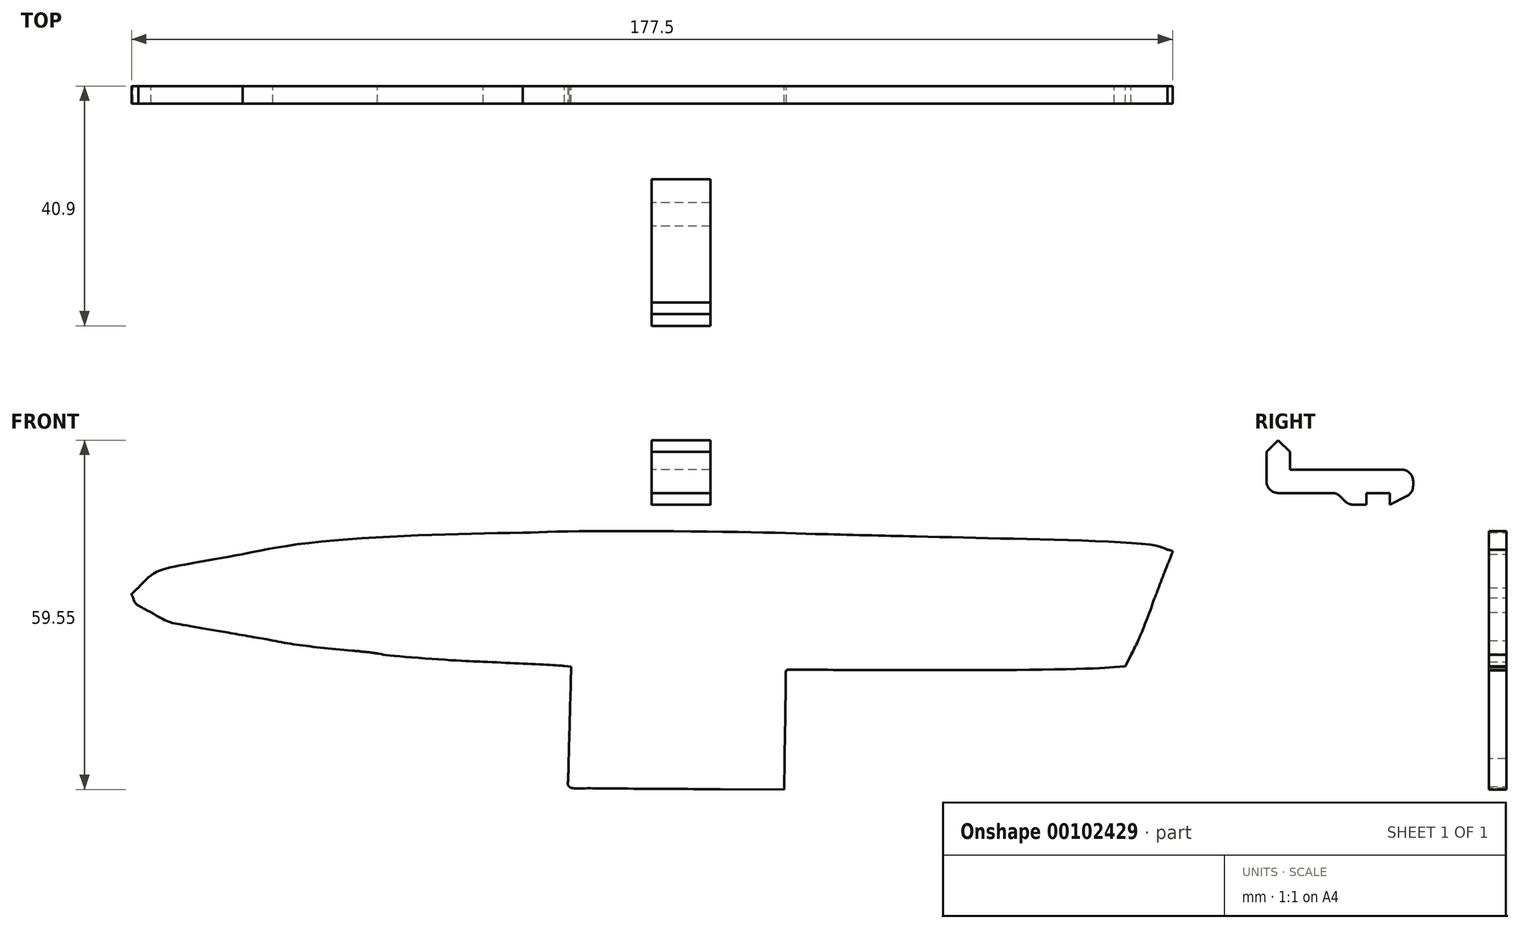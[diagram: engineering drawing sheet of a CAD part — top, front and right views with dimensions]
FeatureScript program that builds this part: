
annotation { "Feature Type Name" : "Feature", "Feature Type Description" : "" }
export const myFeature = defineFeature(function(context is Context, id is Id, definition is map)
    precondition{}
    {
        {
            var Q0;
            Q0=qCreatedBy(makeId("Right.planeOp"),FACE);
            var sketch = newSketch(context, id + "F0", { "sketchPlane" : qUnion([Q0])});
            skLineSegment(sketch, "E0.bottom", {"start": v(-15.9, 32.6) * mm, "end": v(-40.9, 32.6) * mm});
            skLineSegment(sketch, "E0.top", {"start": v(-15.9, 28.6) * mm, "end": v(-40.9, 28.6) * mm});
            skLineSegment(sketch, "E0.left", {"start": v(-15.9, 32.6) * mm, "end": v(-15.9, 28.6) * mm});
            skLineSegment(sketch, "E0.right", {"start": v(-40.9, 32.6) * mm, "end": v(-40.9, 28.6) * mm});
            skLineSegment(sketch, "E1", {"start": v(-15.9, 28.6) * mm, "end": v(-19.9, 26.6) * mm});
            skLineSegment(sketch, "E2", {"start": v(-19.9, 26.6) * mm, "end": v(-19.9, 28.6) * mm});
            skLineSegment(sketch, "E3", {"start": v(-23.9, 28.6) * mm, "end": v(-23.9, 26.6) * mm});
            skLineSegment(sketch, "E4", {"start": v(-23.9, 26.6) * mm, "end": v(-26.9, 26.6) * mm});
            skLineSegment(sketch, "E5", {"start": v(-26.9, 26.6) * mm, "end": v(-28.9, 28.6) * mm});
            skLineSegment(sketch, "E6", {"start": v(-40.9, 32.6) * mm, "end": v(-40.9, 37.6) * mm});
            skLineSegment(sketch, "E7", {"start": v(-40.9, 37.6) * mm, "end": v(-36.9, 37.6) * mm});
            skLineSegment(sketch, "E8", {"start": v(-36.9, 37.6) * mm, "end": v(-36.9, 32.6) * mm});
            skSolve(sketch);
        }
        {
            var Q0;
            Q0=makeQuery(id+"F0.imprint","IMPRINT",FACE,{"disambiguationData":[TD([[makeQuery(id+"F0.imprint","IMPRINT",EDGE,{"derivedFrom":sQuery(id+"F0.wireOp",EDGE,"E0.bottom")}),1.0]])]});
            var Q1;
            {var subQ2=sQuery(id+"F0.wireOp",EDGE,"E3");Q1=makeQuery(id+"F0.imprint","IMPRINT",FACE,{"disambiguationData":[TD([[makeQuery(id+"F0.imprint","IMPRINT",EDGE,{"derivedFrom":subQ2}),-1.0]])]});}
            var Q2;
            {var subQ0=sQuery(id+"F0.wireOp",EDGE,"E1");Q2=makeQuery(id+"F0.imprint","IMPRINT",FACE,{"disambiguationData":[TD([[makeQuery(id+"F0.imprint","IMPRINT",EDGE,{"derivedFrom":subQ0}),-1.0]])]});}
            var Q3;
            {var subQ0=sQuery(id+"F0.wireOp",EDGE,"E6");Q3=makeQuery(id+"F0.imprint","IMPRINT",FACE,{"disambiguationData":[TD([[makeQuery(id+"F0.imprint","IMPRINT",EDGE,{"derivedFrom":subQ0}),-1.0]])]});}
            extrude(context, id + "F1", {"entities" : qUnion([Q0, Q1, Q2, Q3]), "depth" : 10 * mm, "offsetDistance" : 25 * mm});
        }
        {
            var Q0;
            Q0=makeQuery(id+"F1.opExtrude","SWEPT_EDGE",EDGE,{"disambiguationData":[OSD([sQuery(id+"F0.wireOp",EDGE,"E0.top"),sQuery(id+"F0.wireOp",EDGE,"E0.left"),sQuery(id+"F0.wireOp",EDGE,"E1")])]});
            var Q1;
            Q1=makeQuery(id+"F1.opExtrude","SWEPT_EDGE",EDGE,{"disambiguationData":[OSD([sQuery(id+"F0.wireOp",EDGE,"E4"),sQuery(id+"F0.wireOp",EDGE,"E5")])]});
            var Q2;
            Q2=makeQuery(id+"F1.opExtrude","SWEPT_EDGE",EDGE,{"disambiguationData":[OSD([sQuery(id+"F0.wireOp",EDGE,"E0.top"),sQuery(id+"F0.wireOp",EDGE,"E5")])]});
            var Q3;
            Q3=makeQuery(id+"F1.opExtrude","SWEPT_EDGE",EDGE,{"disambiguationData":[OSD([sQuery(id+"F0.wireOp",EDGE,"E0.top"),sQuery(id+"F0.wireOp",EDGE,"E0.right")])]});
            var Q4;
            Q4=makeQuery(id+"F1.opExtrude","SWEPT_EDGE",EDGE,{"disambiguationData":[OSD([sQuery(id+"F0.wireOp",EDGE,"E0.bottom"),sQuery(id+"F0.wireOp",EDGE,"E0.left")])]});
            fillet(context, id + "F2", {"entities" : qUnion([Q0, Q1, Q2, Q3, Q4]), "tangentPropagation" : true, "radius" : 2 * mm, "defaultsChanged" : false, "vertexSettings" : [], "allowEdgeOverflow" : false});
        }
        {
            var Q0;
            Q0=makeQuery(id+"F1.opExtrude","SWEPT_EDGE",EDGE,{"disambiguationData":[OSD([sQuery(id+"F0.wireOp",EDGE,"E7"),sQuery(id+"F0.wireOp",EDGE,"E8")])]});
            var Q1;
            Q1=makeQuery(id+"F1.opExtrude","SWEPT_EDGE",EDGE,{"disambiguationData":[OSD([sQuery(id+"F0.wireOp",EDGE,"E6"),sQuery(id+"F0.wireOp",EDGE,"E7")])]});
            chamfer(context, id + "F3", {"entities" : qUnion([Q0, Q1]), "width" : 2 * mm, "tangentPropagation" : true});
        }
        {
            var Q0;
            Q0=qCreatedBy(makeId("Front.planeOp"),FACE);
            var sketch = newSketch(context, id + "F4", { "sketchPlane" : qUnion([Q0])});
            skLineSegment(sketch, "E9", {"start": v(-13.88, -6.6) * mm, "end": v(-13.75, -1.02) * mm});
            skLineSegment(sketch, "E10", {"start": v(-13.75, -1.02) * mm, "end": v(-14.84, -0.91) * mm});
            skLineSegment(sketch, "E11", {"start": v(81.72, 1) * mm, "end": v(80.75, -0.95) * mm});
            skLineSegment(sketch, "E12", {"start": v(80.75, -0.95) * mm, "end": v(78.87, -1.06) * mm});
            skLineSegment(sketch, "E13", {"start": v(22.75, -11.83) * mm, "end": v(22.6, -21.95) * mm});
            skLineSegment(sketch, "E14", {"start": v(22.6, -21.95) * mm, "end": v(11.7, -21.9) * mm});
            skFitSpline(sketch, "E15", {"points": [v(-6.44, -21.8) * mm, v(-11.8, -21.76) * mm, v(-13.75, -21.68) * mm, v(-13.98, -21.5) * mm]});
            skFitSpline(sketch, "E16", {"points": [v(-13.98, -21.5) * mm, v(-14.23, -21.28) * mm, v(-14.26, -20.59) * mm, v(-14.14, -16.7) * mm]});
            skFitSpline(sketch, "E17", {"points": [v(-14.14, -16.7) * mm, v(-14.07, -14.21) * mm, v(-13.95, -9.66) * mm, v(-13.88, -6.6) * mm]});
            skFitSpline(sketch, "E18", {"points": [v(-14.84, -0.91) * mm, v(-15.93, -0.8) * mm, v(-20.6, -0.55) * mm, v(-28.73, -0.17) * mm]});
            skFitSpline(sketch, "E19", {"points": [v(-28.73, -0.17) * mm, v(-33.54, 0.05) * mm, v(-44.9, 0.93) * mm, v(-46.77, 1.23) * mm]});
            skFitSpline(sketch, "E20", {"points": [v(-46.77, 1.23) * mm, v(-47.44, 1.34) * mm, v(-49.39, 1.56) * mm, v(-51.1, 1.73) * mm]});
            skFitSpline(sketch, "E21", {"points": [v(-51.1, 1.73) * mm, v(-56.94, 2.3) * mm, v(-61.23, 2.84) * mm, v(-64.59, 3.44) * mm]});
            skFitSpline(sketch, "E22", {"points": [v(-64.59, 3.44) * mm, v(-66.43, 3.77) * mm, v(-70.81, 4.54) * mm, v(-74.33, 5.16) * mm]});
            skFitSpline(sketch, "E23", {"points": [v(-74.33, 5.16) * mm, v(-81.16, 6.35) * mm, v(-82.61, 6.76) * mm, v(-85.34, 8.23) * mm]});
            skFitSpline(sketch, "E24", {"points": [v(-85.34, 8.23) * mm, v(-87.38, 9.34) * mm, v(-88.07, 9.9) * mm, v(-88.41, 10.74) * mm]});
            skFitSpline(sketch, "E25", {"points": [v(-88.41, 10.74) * mm, v(-88.68, 11.37) * mm, v(-88.67, 11.39) * mm, v(-87.52, 12.46) * mm]});
            skFitSpline(sketch, "E26", {"points": [v(-87.52, 12.46) * mm, v(-84.94, 14.86) * mm, v(-81, 16.12) * mm, v(-69.75, 18.15) * mm]});
            skFitSpline(sketch, "E27", {"points": [v(-69.75, 18.15) * mm, v(-60.42, 19.83) * mm, v(-40.82, 21.34) * mm, v(-21.98, 21.82) * mm]});
            skFitSpline(sketch, "E28", {"points": [v(-21.98, 21.82) * mm, v(-12.38, 22.06) * mm, v(14.54, 21.95) * mm, v(27.92, 21.61) * mm]});
            skFitSpline(sketch, "E29", {"points": [v(27.92, 21.61) * mm, v(32.52, 21.5) * mm, v(40.23, 21.3) * mm, v(45.05, 21.19) * mm]});
            skFitSpline(sketch, "E30", {"points": [v(45.05, 21.19) * mm, v(66.35, 20.68) * mm, v(85.68, 19.67) * mm, v(87.94, 18.95) * mm]});
            skFitSpline(sketch, "E31", {"points": [v(87.94, 18.95) * mm, v(88.8, 18.68) * mm, v(88.78, 18.44) * mm, v(87.77, 15.9) * mm]});
            skFitSpline(sketch, "E32", {"points": [v(87.77, 15.9) * mm, v(87.31, 14.76) * mm, v(86.4, 12.4) * mm, v(85.75, 10.64) * mm]});
            skFitSpline(sketch, "E33", {"points": [v(85.75, 10.64) * mm, v(84.1, 6.23) * mm, v(82.87, 3.29) * mm, v(81.72, 1) * mm]});
            skFitSpline(sketch, "E34", {"points": [v(78.87, -1.06) * mm, v(74.34, -1.35) * mm, v(54.7, -1.6) * mm, v(39.54, -1.58) * mm]});
            skFitSpline(sketch, "E35", {"points": [v(39.54, -1.58) * mm, v(30.47, -1.56) * mm, v(23.01, -1.59) * mm, v(22.97, -1.63) * mm]});
            skFitSpline(sketch, "E36", {"points": [v(22.97, -1.63) * mm, v(22.92, -1.68) * mm, v(22.82, -6.27) * mm, v(22.75, -11.83) * mm]});
            skFitSpline(sketch, "E37", {"points": [v(11.7, -21.9) * mm, v(5.7, -21.88) * mm, v(-2.46, -21.83) * mm, v(-6.44, -21.8) * mm]});
            skSolve(sketch);
        }
        {
            var Q0;
            Q0=makeQuery(id+"F4.imprint","IMPRINT",FACE,{"disambiguationData":[TD([[makeQuery(id+"F4.imprint","IMPRINT",EDGE,{"derivedFrom":sQuery(id+"F4.wireOp",EDGE,"E9")}),-1.0]])]});
            extrude(context, id + "F5", {"entities" : qUnion([Q0]), "depth" : 3 * mm, "offsetDistance" : 25 * mm});
        }
    });
